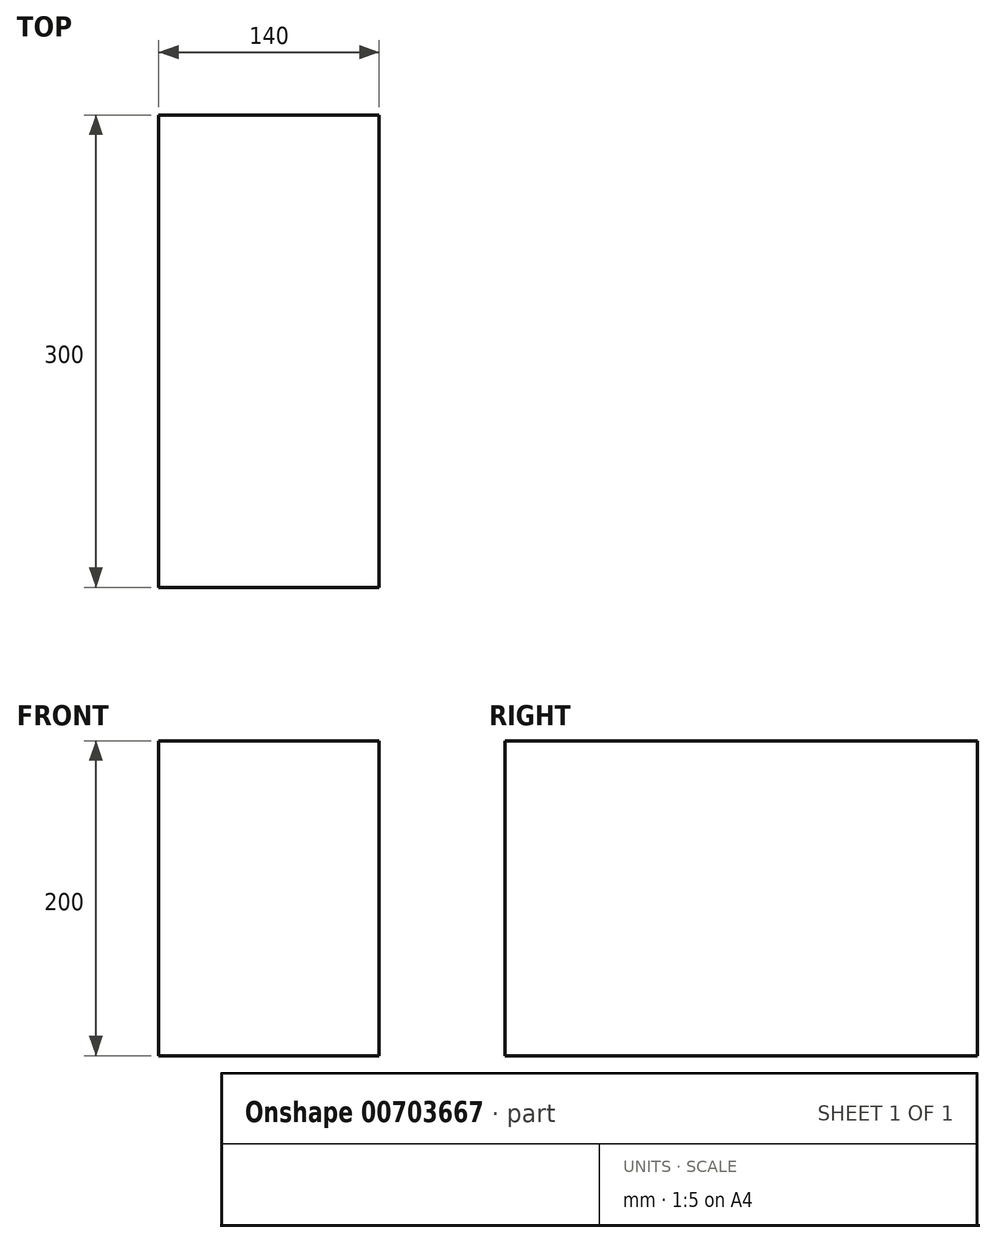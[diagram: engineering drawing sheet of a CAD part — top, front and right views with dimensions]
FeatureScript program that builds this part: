
annotation { "Feature Type Name" : "Feature", "Feature Type Description" : "" }
export const myFeature = defineFeature(function(context is Context, id is Id, definition is map)
    precondition{}
    {
        {
            var Q0;
            Q0=qCreatedBy(makeId("Front.planeOp"),FACE);
            var sketch = newSketch(context, id + "F0", { "sketchPlane" : qUnion([Q0])});
            skLineSegment(sketch, "E0.bottom", {"start": v(-70, 100) * mm, "end": v(70, 100) * mm});
            skLineSegment(sketch, "E0.top", {"start": v(-70, -100) * mm, "end": v(70, -100) * mm});
            skLineSegment(sketch, "E0.left", {"start": v(-70, 100) * mm, "end": v(-70, -100) * mm});
            skLineSegment(sketch, "E0.right", {"start": v(70, 100) * mm, "end": v(70, -100) * mm});
            skSolve(sketch);
        }
        {
            var Q0;
            Q0=makeQuery(id+"F0.imprint","IMPRINT",FACE,{"disambiguationData":[TD([[makeQuery(id+"F0.imprint","IMPRINT",EDGE,{"derivedFrom":sQuery(id+"F0.wireOp",EDGE,"E0.bottom")}),-1.0]])]});
            extrude(context, id + "F1", {"entities" : qUnion([Q0]), "oppositeDirection" : true, "depth" : 300 * mm, "offsetDistance" : 25 * mm});
        }
    });
